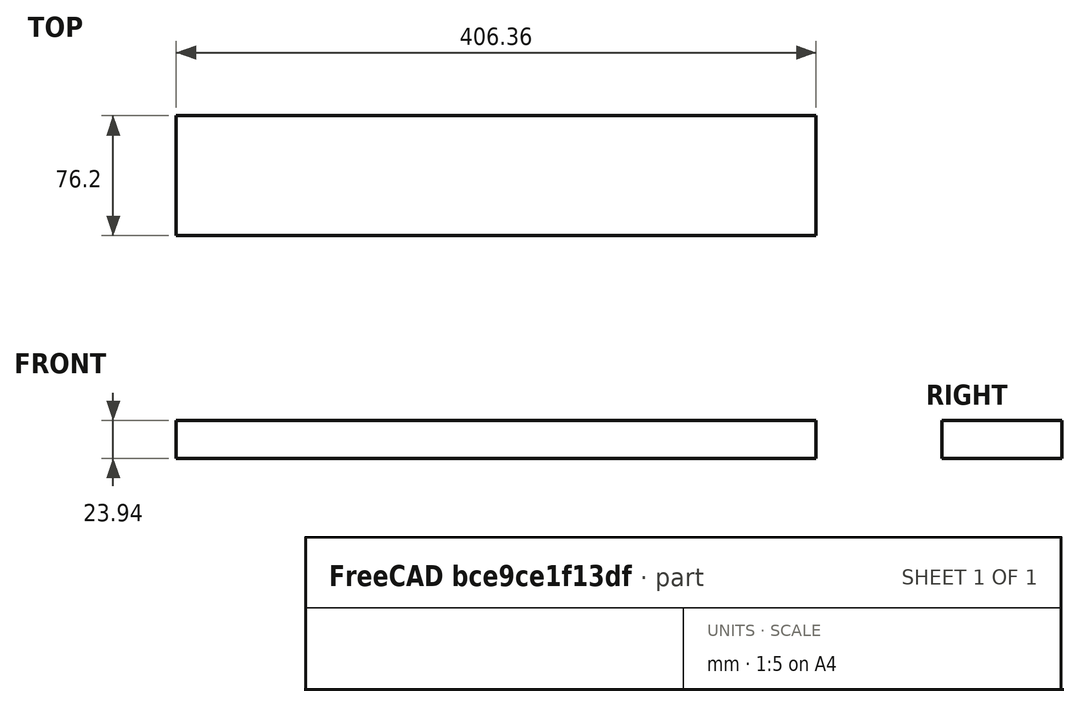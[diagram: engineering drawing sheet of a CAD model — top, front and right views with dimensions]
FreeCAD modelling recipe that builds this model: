
FCSTD DOCUMENT  (FreeCAD 0.19R24276 (Git))
Label: cover side
License: All rights reserved
LicenseURL: http://en.wikipedia.org/wiki/All_rights_reserved
objects: Sketcher::SketchObject×1, PartDesign::Pad×1, PartDesign::Body×1
note: 4 computed .brp shape members not serialized (recipe doc carries the construction recipe); baked Part::Feature solids carry a one-line shape summary decoded from their .brp

FEATURE [Sketcher::SketchObject] Sketch
  FullyConstrained = true
  MapMode = 5
  Support = -> [XY_Plane]
  sketch-geometry (4):
    g0: LineSegment StartX=0 StartY=0 StartZ=0 EndX=406.36 EndY=0 EndZ=0
    g1: LineSegment StartX=406.36 StartY=0 StartZ=0 EndX=406.36 EndY=-76.2 EndZ=0
    g2: LineSegment StartX=406.36 StartY=-76.2 StartZ=0 EndX=0 EndY=-76.2 EndZ=0
    g3: LineSegment StartX=0 StartY=-76.2 StartZ=0 EndX=0 EndY=0 EndZ=0
  constraints (11):
    c: Coincident(g0,g1)
    c: Coincident(g1,g2)
    c: Coincident(g2,g3)
    c: Coincident(g3,g0)
    c: Horizontal(g0)
    c: Horizontal(g2)
    c: Vertical(g1)
    c: Vertical(g3)
    c: Coincident(g0,g-1)
    c: DistanceY(g1,g1) = 76.2
    c: DistanceX(g0,g0) = 406.36
FEATURE [PartDesign::Pad] Pad
  Direction = (1,1,1)
  Length = 23.94
  Length2 = 100
  Profile = -> Sketch
  Type = 0
FEATURE [PartDesign::Body] Body
  Group = -> [Sketch,Pad]
  Origin = -> Origin
  Tip = -> Pad
